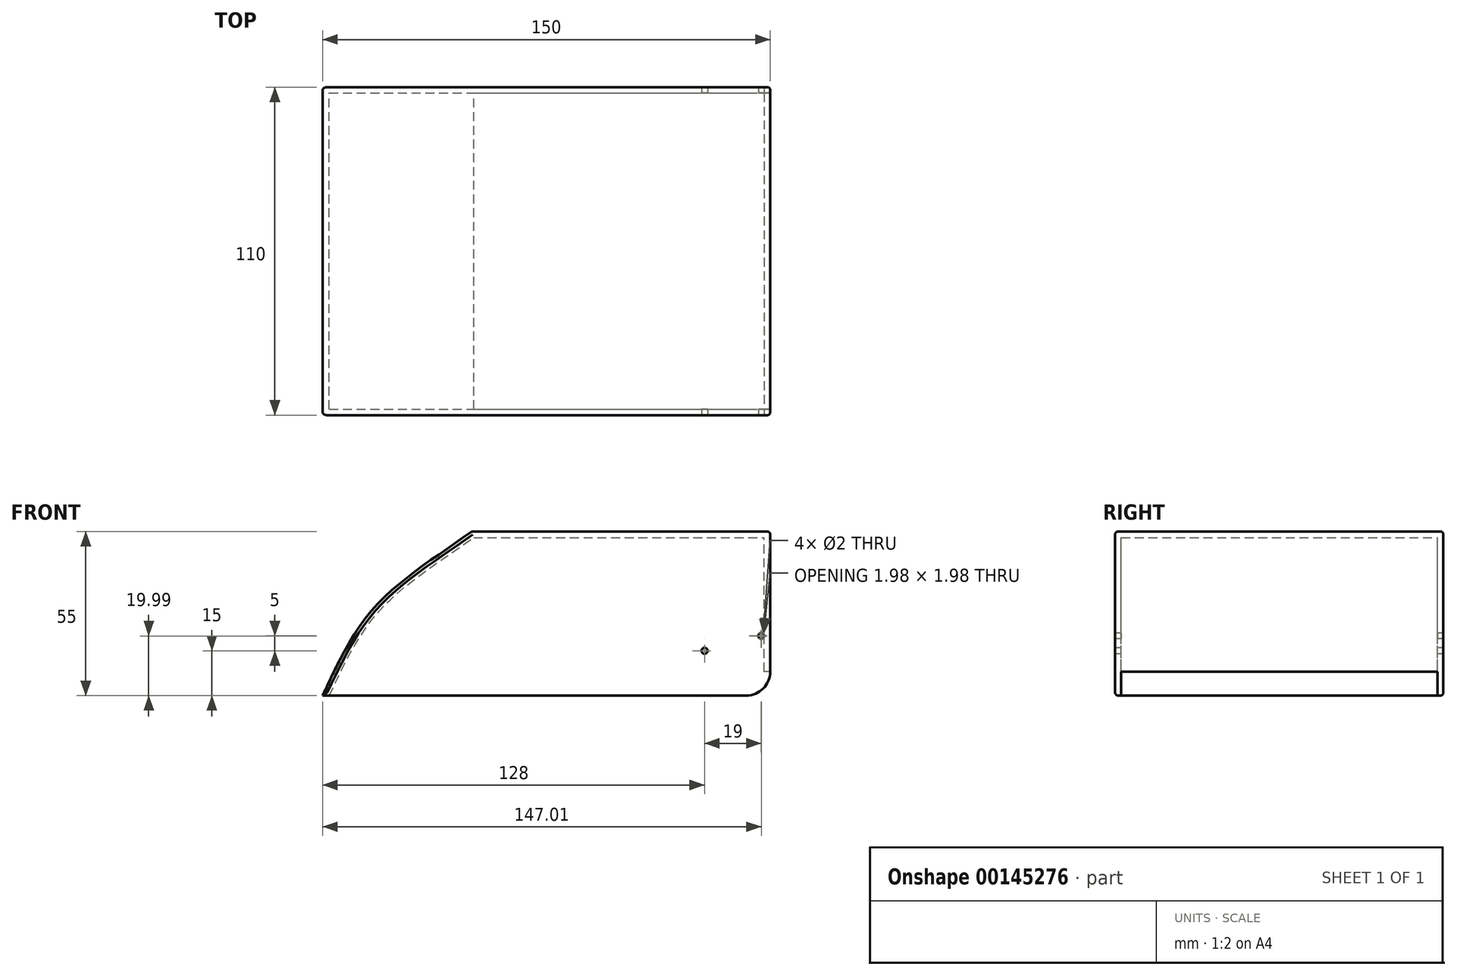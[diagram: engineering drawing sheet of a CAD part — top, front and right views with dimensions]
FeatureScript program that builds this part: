
annotation { "Feature Type Name" : "Feature", "Feature Type Description" : "" }
export const myFeature = defineFeature(function(context is Context, id is Id, definition is map)
    precondition{}
    {
        {
            var Q0;
            Q0=qCreatedBy(makeId("Front.planeOp"),FACE);
            var sketch = newSketch(context, id + "F0", { "sketchPlane" : qUnion([Q0])});
            skLineSegment(sketch, "E0.bottom", {"start": v(0, 0) * mm, "end": v(142, 0) * mm});
            skLineSegment(sketch, "E0.top", {"start": v(50, 55) * mm, "end": v(150, 55) * mm});
            skLineSegment(sketch, "E0.right", {"start": v(150, 8) * mm, "end": v(150, 55) * mm});
            skFitSpline(sketch, "E1", {"points": [v(0, 0) * mm, v(17.44, 29.63) * mm, v(50, 55) * mm], "startDerivative": vector(30.77, 64.24) * mm, "endDerivative": vector(63.74, 45.96) * mm});
            skPoint(sketch, "E2.visualSharp", {"position": v(150, 0) * mm});
            skArc(sketch, "E2.filletArc", {"start": v(142, 0) * mm, "mid": v(147.66, 2.34) * mm, "end": v(150, 8) * mm});
            skSolve(sketch);
        }
        {
            var Q0;
            Q0=makeQuery(id+"F0.imprint","IMPRINT",FACE,{"disambiguationData":[TD([[makeQuery(id+"F0.imprint","IMPRINT",EDGE,{"derivedFrom":sQuery(id+"F0.wireOp",EDGE,"E0.bottom")}),1.0]])]});
            extrude(context, id + "F1", {"entities" : qUnion([Q0]), "depth" : 110 * mm});
        }
        {
            var Q0;
            Q0=makeQuery(id+"F1.opExtrude","CAP_FACE",FACE,{"disambiguationData":[OSD([sQuery(id+"F0.wireOp",EDGE,"E0.bottom"),sQuery(id+"F0.wireOp",EDGE,"E0.top"),sQuery(id+"F0.wireOp",EDGE,"E0.right"),sQuery(id+"F0.wireOp",EDGE,"E1")])],"isStart":false});
            var sketch = newSketch(context, id + "F2", { "sketchPlane" : qUnion([Q0])});
            skCircle(sketch, "E3", {"center": v(147, 20) * mm, "radius": 1 * mm});
            skSolve(sketch);
        }
        {
            var Q0;
            Q0=makeQuery(id+"F1.opExtrude","SWEPT_FACE",FACE,{"disambiguationData":[OSD([sQuery(id+"F0.wireOp",EDGE,"E0.bottom")])]});
            var Q1;
            Q1=makeQuery(id+"F1.opExtrude","SWEPT_FACE",FACE,{"disambiguationData":[OSD([sQuery(id+"F0.wireOp",EDGE,"E2.filletArc")])]});
            shell(context, id + "F3", {"entities" : qUnion([Q0, Q1]), "thickness" : 2 * mm});
        }
        {
            var Q0;
            Q0=makeQuery(id+"F2.imprint","IMPRINT",FACE,{"disambiguationData":[TD([[makeQuery(id+"F2.imprint","IMPRINT",EDGE,{"derivedFrom":sQuery(id+"F2.wireOp",EDGE,"E3")}),1.0]])]});
            extrude(context, id + "F4", {"entities" : qUnion([Q0]), "operationType" : NewBodyOperationType.REMOVE, "endBound" : BoundingType.THROUGH_ALL, "oppositeDirection" : true, "depth" : 25 * mm});
        }
        {
            var Q0;
            Q0=makeQuery(id+"F1.opExtrude","CAP_FACE",FACE,{"disambiguationData":[OSD([sQuery(id+"F0.wireOp",EDGE,"E0.bottom"),sQuery(id+"F0.wireOp",EDGE,"E0.top"),sQuery(id+"F0.wireOp",EDGE,"E0.right"),sQuery(id+"F0.wireOp",EDGE,"E1"),sQuery(id+"F0.wireOp",EDGE,"E2.filletArc")])],"isStart":false});
            var sketch = newSketch(context, id + "F5", { "sketchPlane" : qUnion([Q0])});
            skCircle(sketch, "E4", {"center": v(128, 15) * mm, "radius": 1 * mm});
            skSolve(sketch);
        }
        {
            var Q0;
            Q0 = qSketchRegion(id + "F5", true);
            extrude(context, id + "F6", {"entities" : qUnion([Q0]), "operationType" : NewBodyOperationType.REMOVE, "endBound" : BoundingType.THROUGH_ALL, "oppositeDirection" : true, "depth" : 2 * mm});
        }
        {
            var Q0;
            Q0=makeQuery(id+"F1.opExtrude","SWEPT_EDGE",EDGE,{"disambiguationData":[OSD([sQuery(id+"F0.wireOp",EDGE,"E0.top"),sQuery(id+"F0.wireOp",EDGE,"E1")])]});
            var Q1;
            Q1=makeQuery(id+"F1.opExtrude","CAP_EDGE",EDGE,{"disambiguationData":[OSD([sQuery(id+"F0.wireOp",EDGE,"E0.top")])],"isStart":true});
            var Q2;
            Q2=makeQuery(id+"F1.opExtrude","CAP_EDGE",EDGE,{"disambiguationData":[OSD([sQuery(id+"F0.wireOp",EDGE,"E0.top")])],"isStart":false});
            var Q3;
            Q3=makeQuery(id+"F1.opExtrude","SWEPT_EDGE",EDGE,{"disambiguationData":[OSD([sQuery(id+"F0.wireOp",EDGE,"E0.top"),sQuery(id+"F0.wireOp",EDGE,"E0.right")])]});
            var Q4;
            Q4=makeQuery(id+"F1.opExtrude","CAP_EDGE",EDGE,{"disambiguationData":[OSD([sQuery(id+"F0.wireOp",EDGE,"E1")])],"isStart":false});
            var Q5;
            Q5=makeQuery(id+"F1.opExtrude","CAP_EDGE",EDGE,{"disambiguationData":[OSD([sQuery(id+"F0.wireOp",EDGE,"E1")])],"isStart":true});
            var Q6;
            Q6=makeQuery(id+"F1.opExtrude","CAP_EDGE",EDGE,{"disambiguationData":[OSD([sQuery(id+"F0.wireOp",EDGE,"E0.right")])],"isStart":false});
            var Q7;
            Q7=makeQuery(id+"F1.opExtrude","CAP_EDGE",EDGE,{"disambiguationData":[OSD([sQuery(id+"F0.wireOp",EDGE,"E0.right")])],"isStart":true});
            fillet(context, id + "F7", {"entities" : qUnion([Q0, Q1, Q2, Q3, Q4, Q5, Q6, Q7]), "radius" : 1 * mm, "tangentPropagation" : true, "allowEdgeOverflow" : false});
        }
    });
